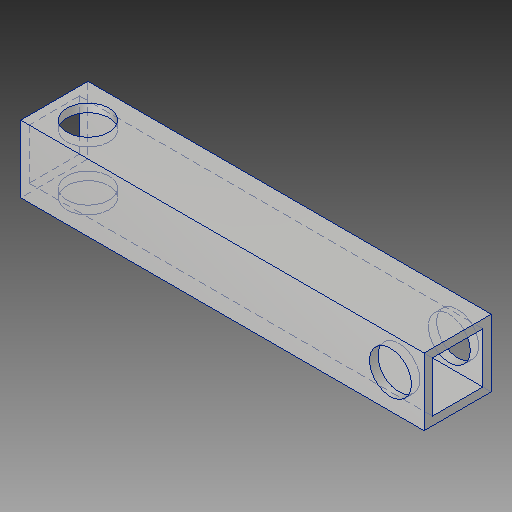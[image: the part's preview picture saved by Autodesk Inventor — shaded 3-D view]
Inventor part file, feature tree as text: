
AUTODESK INVENTOR PART (.ipt)
format: ipt  version: 2019 (Build 230136000, 136)  size: 123,904 bytes
history: native  units: in
note: dims shown in document units (in); Inventor stores cm internally (conversion verified against a paired STEP export)
features: extrude x3, sketch x3
ambient origin geometry x8: Origin, YZ Plane, XZ Plane, XY Plane, X Axis, Y Axis, Z Axis, Center Point
bodies: Solid1 (feature_tree)
feature tree (6):
  extrude  "Extrusion1"  Depth=1.0in
  extrude  "Extrusion2"  Depth=6.0in
  extrude  "Extrusion3"  Depth=5.0in TaperAngle=0.0deg
  sketch  "Sketch1"  dims[d0=0.125in d1=1.0in]
  sketch  "Sketch2"  dims[d2=6.0in d3=0.0in d4=0.625in]
  sketch  "Sketch3"  dims[d5=0.5in d6=5.0in d7=0.0in d8=0.5in d9=0.625in d10=5.0in d11=0.0in]
